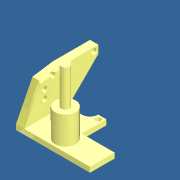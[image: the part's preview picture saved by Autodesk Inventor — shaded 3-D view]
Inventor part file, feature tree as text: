
AUTODESK INVENTOR PART (.ipt)
format: ipt  version: 2020 (Build 240168000, 168)  size: 306,176 bytes
history: native  units: mm
features: sketch x13, extrude x12, chamfer x3, projected_geometry x3, plane x1, pattern_circular x1, loft x1, fillet x1, other x1
ambient origin geometry x8: Origin, YZ Plane, XZ Plane, XY Plane, X Axis, Y Axis, Z Axis, Center Point
bodies: Solid1 (feature_tree)
feature tree (36):
  plane  "Work Plane1"
  extrude  "Extrusion1"  Depth=32.0mm TaperAngle=0.0deg
  extrude  "Extrusion3"  Depth=27.0mm TaperAngle=0.0deg
  extrude  "Extrusion9"  Depth=24.0mm
  pattern_circular  "Circular Pattern1"  Count=4 Angle=360.0deg
  extrude  "Extrusion11"  Depth=8.0mm
  extrude  "Extrusion12"  Depth=8.0mm
  chamfer  "Chamfer4"  Distance=48.0mm
  chamfer  "Chamfer5"  Distance=32.0mm Angle=45.0deg
  chamfer  "Chamfer6"  Distance=20.0mm Angle=45.0deg
  extrude  "Extrusion13"  Depth=6.0mm TaperAngle=0.0deg
  loft  "Loft1"
  extrude  "Extrusion14"  Depth=4.8mm
  fillet  "Fillet1"  Radius=4.8mm
  extrude  "Extrusion15"  Depth=4.8mm
  extrude  "Extrusion16"  Depth=8.0mm
  extrude  "Extrusion17"  Depth=8.0mm
  extrude  "Extrusion19"  Depth=32.0mm
  extrude  "Extrusion20"  Depth=5.0mm
  sketch  "Sketch1"  dims[d0=8.0mm d2=32.0mm d3=0.0mm]
  sketch  "Sketch5"  dims[d17=20.0mm d18=27.0mm d19=0.0mm]
  sketch  "Sketch17"  dims[d86=72.0mm d87=24.0mm]
  sketch  "Sketch19"  dims[d88=5.0mm d89=0.0mm d93=40.0mm d94=360.0deg]
  sketch  "Sketch20"  dims[d103=8.0mm d104=8.0mm]
  sketch  "Sketch21"  dims[d105=35.0mm d106=0.0mm d107=8.0mm]
  sketch  "Sketch23"  dims[d108=40.0mm d109=48.0mm d110=0.0mm d111=32.0mm d112=20.0mm d113=45.0deg d114=20.0mm d115=3.0mm d116=45.0deg]
  other  "Edges1"
  sketch  "Sketch24"  dims[d117=2.0mm d118=3.0mm d119=45.0deg d120=6.0mm d121=0.0mm]
  sketch  "Sketch25"  dims[d122=0.0mm d123=90.0deg d124=0.0mm d125=90.0deg]
  sketch  "Sketch27"  dims[d126=4.8mm d127=4.8mm d128=4.8mm]
  projected_geometry  "Projected Loop1"
  sketch  "Sketch28"  dims[d129=4.8mm d130=4.8mm]
  projected_geometry  "Projected Loop2"
  sketch  "Sketch31"  dims[d131=8.0mm d132=8.0mm]
  projected_geometry  "Projected Loop4"
  sketch  "Sketch33"  dims[d133=8.0mm d134=8.0mm d135=32.0mm d136=20.0mm d137=16.0mm d138=0.0mm d139=0.7mm d140=4.8mm d141=32.0mm d142=16.0mm d143=0.0mm d144=32.0mm d145=0.0mm d146=8.0mm d147=0.0mm d154=8.0mm d155=0.0mm d156=16.0mm d157=5.0mm d158=0.0mm d161=0.5mm d162=0.872665mm d163=0.5mm d164=0.872665mm]
